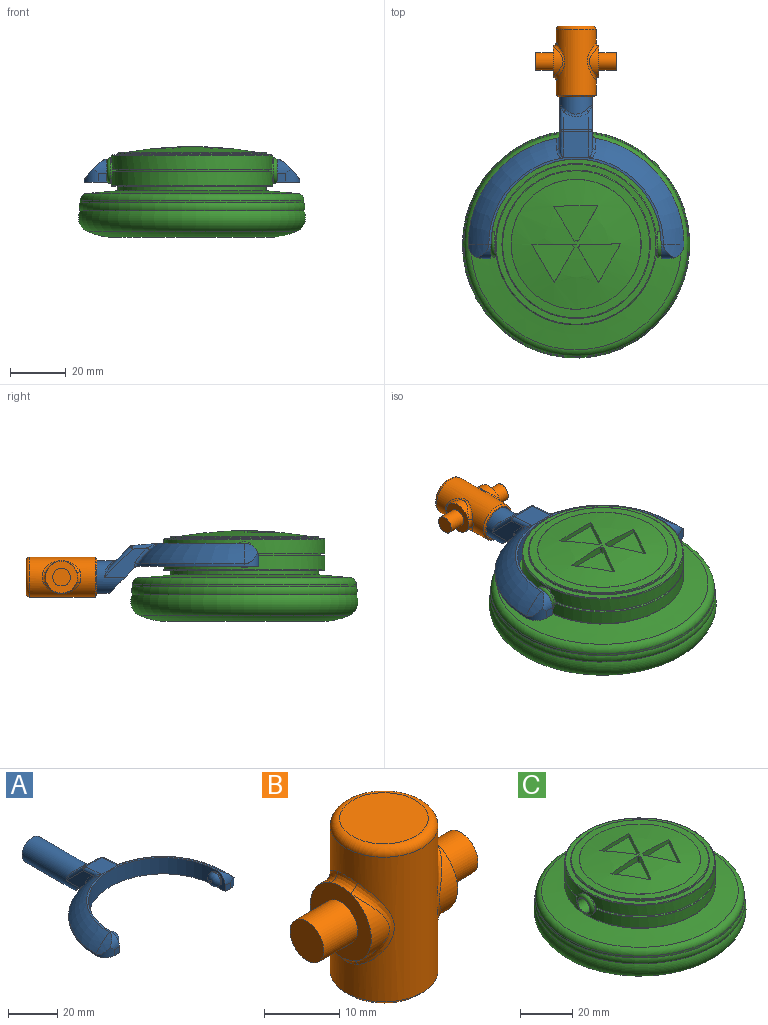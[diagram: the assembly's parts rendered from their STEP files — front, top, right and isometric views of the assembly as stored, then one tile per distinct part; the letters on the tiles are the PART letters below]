
ASSEMBLY  parts=3 mates=2
PART A: 48 faces, bbox 77.3x80.8x18.2 mm
  f0: plane 11.99x9.83mm, normal (0,-0.71,-0.71), area 141.5mm2, adj f1,f2,f9,f30,f43,f46
  f1: plane 15.39x10.49mm, normal (-1,0,0), area 63.5mm2, adj f0,f30,f32,f36,f46,f47
  f2: plane 15.39x10.49mm, normal (1,0,0), area 63.5mm2, adj f0,f30,f34,f39,f43,f44
  f3: plane 9.14x6.37mm, normal (0,0.71,0.71), area 67.6mm2, adj f35,f36,f39,f40
  f4: cylinder r=38.61mm len=37.99mm, axis (0,0,-1), area 42.6mm2, adj f6,f9,f17,f46,f47
  f5: torus R=19.3mm, axis (0,0,-1), area 507.8mm2, adj f10,f11,f12,f29,f42,f44
  f6: torus R=19.3mm, axis (0,0,-1), area 507.8mm2, adj f4,f11,f15,f28,f45,f47
  f7: cylinder r=30.48mm len=60.96mm, axis (0,0,-1), area 746.6mm2, adj f8,f9,f11,f14,f21,f24
  f8: plane 8.13x5.08mm, normal (-1,0,0), area 19.9mm2, adj f7,f9,f13,f19,f24
  f9: plane 77.22x43.73mm, normal (0,0,-1), area 956.2mm2, adj f0,f4,f7,f8,f10,f13,f14,f16
  f10: cylinder r=38.61mm len=37.99mm, axis (0,0,-1), area 42.6mm2, adj f5,f9,f20,f43,f44
  f11: plane 62.55x30.95mm, normal (0,0,1), area 75mm2, adj f5,f6,f7,f18,f19,f27
  f12: cylinder r=22.71mm len=7.33mm, axis (0,1,0), area 24.8mm2, adj f5,f19,f20
  f13: plane 3.05x3.05mm, normal (0,-1,0), area 9.3mm2, adj f8,f9,f19,f20
  f14: plane 8.13x5.08mm, normal (1,0,0), area 19.9mm2, adj f7,f9,f16,f18,f21
  f15: cylinder r=22.71mm len=7.33mm, axis (0,1,0), area 24.8mm2, adj f6,f17,f18
  f16: plane 3.05x3.05mm, normal (0,-1,0), area 9.3mm2, adj f9,f14,f17,f18
  f17: cylinder r=5.08mm len=5.08mm, axis (0,0,-1), area 21.9mm2, adj f4,f9,f15,f16,f18
  f18: cylinder r=5.08mm len=5.08mm, axis (-1,0,0), area 21.9mm2, adj f11,f14,f15,f16,f17
  f19: cylinder r=5.08mm len=5.08mm, axis (-1,0,0), area 21.9mm2, adj f8,f11,f12,f13,f20
  f20: cylinder r=5.08mm len=5.08mm, axis (0,0,-1), area 21.9mm2, adj f9,f10,f12,f13,f19
  f21: cylinder r=3.17mm len=6.35mm, axis (-1,0,0), area 12.7mm2, adj f7,f14,f23
  f22: plane 1.27x1.27mm, normal (1,0,0), area 1.3mm2, adj f23
  f23: torus R=0.64mm, axis (1,0,0), area 56.5mm2, adj f21,f22
  f24: cylinder r=3.17mm len=6.35mm, axis (1,0,0), area 12.7mm2, adj f7,f8,f26
  f25: plane 1.27x1.27mm, normal (-1,0,0), area 1.3mm2, adj f26
  f26: torus R=0.64mm, axis (-1,0,0), area 56.5mm2, adj f24,f25
  f27: plane 9.86x9.36mm, normal (0,0.09,1), area 85.6mm2, adj f11,f28,f29,f32,f34,f35,f42,f45
  f28: plane 1.04x0.17mm, normal (0,-1,0), area 0mm2, adj f6,f27,f45
  f29: plane 1.04x0.17mm, normal (0,-1,0), area 0mm2, adj f5,f27,f42
  f30: cylinder r=5.84mm len=33.01mm, axis (0,-1,0), area 1029.7mm2, adj f0,f1,f2,f31,f38,f40,f41
  f31: plane 11.68x11.68mm, normal (0,1,0), area 107.2mm2, adj f30
  f32: cylinder r=1.27mm len=9.13mm, axis (0,-1,0.09), area 14.4mm2, adj f1,f27,f33,f45
  f33: sphere r=1.27mm, area 1.5mm2, adj f32,f35,f36
  f34: cylinder r=1.27mm len=9.13mm, axis (0,1,-0.09), area 14.4mm2, adj f2,f27,f37,f42
  f35: cylinder r=1.27mm len=9.14mm, axis (-1,0,0), area 8.1mm2, adj f3,f27,f33,f37
  f36: cylinder r=1.27mm len=10.91mm, axis (0,-0.71,0.71), area 23.1mm2, adj f1,f3,f33,f38
  f37: sphere r=1.27mm, area 1.5mm2, adj f34,f35,f39
  f38: bspline ~4.55x2.75mm, area 2.3mm2, adj f30,f36,f40
  f39: cylinder r=1.27mm len=10.91mm, axis (0,0.71,-0.71), area 23.1mm2, adj f2,f3,f37,f41
  f40: bspline ~9.14x2.56mm, area 10.7mm2, adj f3,f30,f38,f41
  f41: bspline ~5.23x3.53mm, area 2.3mm2, adj f30,f39,f40
  f42: bspline ~4.62x3.14mm, area 5.2mm2, adj f5,f27,f29,f34,f44
  f43: cylinder r=1.27mm len=1.74mm, axis (0,0,-1), area 1.9mm2, adj f0,f2,f9,f10,f44
  f44: bspline ~8.6x7.86mm, area 11.9mm2, adj f2,f5,f10,f42,f43
  f45: bspline ~4.62x3.14mm, area 5.2mm2, adj f6,f27,f28,f32,f47
  f46: cylinder r=1.27mm len=1.74mm, axis (0,0,-1), area 1.9mm2, adj f0,f1,f4,f9,f47
  f47: bspline ~8.6x7.86mm, area 11.9mm2, adj f1,f4,f6,f45,f46
PART B: 25 faces, bbox 28.9x15.5x25.4 mm
  f0: cylinder r=5.71mm len=10.81mm, axis (-1,0,0), area 26.2mm2, adj f5,f15
  f1: cylinder r=5.71mm len=10.81mm, axis (-1,0,0), area 26.2mm2, adj f8,f11
  f2: cylinder r=7.14mm len=23.5mm, axis (0,0,-1), area 763.2mm2, adj f9,f10,f11,f12,f13,f14,f15,f16
  f3: plane 11.75x11.75mm, normal (0,0,1), area 108.4mm2, adj f17
  f4: plane 13.02x13.02mm, normal (0,0,-1), area 16.3mm2, adj f22,f24
  f5: plane 11.46x11.46mm, normal (1,0,0), area 70.9mm2, adj f0,f6,f13,f16,f18
  f6: cylinder r=5.71mm len=10.81mm, axis (-1,0,0), area 26.2mm2, adj f5,f14
  f7: cylinder r=5.71mm len=10.81mm, axis (-1,0,0), area 26.2mm2, adj f8,f10
  f8: plane 11.46x11.46mm, normal (-1,0,0), area 70.9mm2, adj f1,f7,f9,f12,f20
  f9: bspline ~4.64x1.73mm, area 6.5mm2, adj f2,f8,f10,f11
  f10: bspline ~13.62x4.91mm, area 20.7mm2, adj f2,f7,f9,f12
  f11: bspline ~13.6x4.87mm, area 20.7mm2, adj f1,f2,f9,f12
  f12: bspline ~4.64x1.73mm, area 6.5mm2, adj f2,f8,f10,f11
  f13: bspline ~4.64x1.73mm, area 6.5mm2, adj f2,f5,f14,f15
  f14: bspline ~13.62x4.91mm, area 20.7mm2, adj f2,f6,f13,f16
  f15: bspline ~13.6x4.87mm, area 20.7mm2, adj f0,f2,f13,f16
  f16: bspline ~4.64x1.73mm, area 6.5mm2, adj f2,f5,f14,f15
  f17: torus R=5.87mm, axis (0,0,1), area 83.8mm2, adj f2,f3
  f18: cylinder r=3.17mm len=6.35mm, axis (-1,0,0), area 126.7mm2, adj f5,f19
  f19: plane 6.35x6.35mm, normal (1,0,0), area 31.7mm2, adj f18
  f20: cylinder r=3.17mm len=6.35mm, axis (1,0,0), area 126.7mm2, adj f8,f21
  f21: plane 6.35x6.35mm, normal (-1,0,0), area 31.7mm2, adj f20
  f22: cylinder r=6.1mm len=22.86mm, axis (0,0,-1), area 875.6mm2, adj f4,f23
  f23: plane 12.19x12.19mm, normal (0,0,-1), area 116.7mm2, adj f22
  f24: cone r=7.14mm half-angle=45deg, axis (0,0,1), area 38.5mm2, adj f2,f4
PART C: 48 faces, bbox 96.2x96.2x32.5 mm
  f0: cylinder r=28.88mm len=57.76mm, axis (0,0,-1), area 856mm2, adj f1,f2,f38,f39,f44
  f1: plane 57.03x24.32mm, normal (0,0,1), area 101.1mm2, adj f0,f3,f38,f39
  f2: plane 57.03x24.32mm, normal (0,0,1), area 101.1mm2, adj f0,f4,f38,f39
  f3: cylinder r=27.61mm len=54.46mm, axis (0,0,-1), area 49.3mm2, adj f1,f6,f38,f39
  f4: cylinder r=27.61mm len=54.46mm, axis (0,0,-1), area 49.3mm2, adj f2,f5,f38,f39
  f5: plane 57.03x24.32mm, normal (0,0,-1), area 101.1mm2, adj f4,f7,f38,f39
  f6: plane 57.03x24.32mm, normal (0,0,-1), area 101.1mm2, adj f3,f7,f38,f39
  f7: cylinder r=28.88mm len=57.76mm, axis (0,0,-1), area 856mm2, adj f5,f6,f38,f39,f45
  f8: sphere r=135.39mm, area 1385.3mm2, adj f22,f23,f24,f25,f27,f28,f29,f30
  f9: plane 39.33x39.33mm, normal (0,0,-1), area 1214.6mm2, adj f10
  f10: torus R=20.12mm, axis (0,0,-1), area 1429.3mm2, adj f9,f11
  f11: torus R=27.74mm, axis (0,0,-1), area 3542.1mm2, adj f10,f12
  f12: torus R=35.36mm, axis (0,0,-1), area 2180.1mm2, adj f11,f13
  f13: torus R=37.35mm, axis (0,0,-1), area 734.6mm2, adj f12,f14
  f14: cylinder r=40.06mm len=80.11mm, axis (0,0,-1), area 213.3mm2, adj f13,f18
  f15: cone r=26.57mm half-angle=85deg, axis (0,0,-1), area 2265mm2, adj f16,f18
  f16: cylinder r=26.57mm len=53.14mm, axis (0,0,-1), area 265mm2, adj f15,f17
  f17: plane 57.25x57.25mm, normal (0,0,-1), area 356.7mm2, adj f16,f44
  f18: torus R=37.52mm, axis (0,0,1), area 928.6mm2, adj f14,f15
  f19: cone r=26.57mm half-angle=87deg, axis (0,0,-1), area 475.4mm2, adj f46,f47
  f20: cylinder r=26.57mm len=53.14mm, axis (0,0,-1), area 92.3mm2, adj f21,f46
  f21: plane 57.25x57.25mm, normal (0,0,1), area 356.7mm2, adj f20,f45
  f22: cylinder r=1.27mm len=2.53mm, axis (0,0,1), area 3.4mm2, adj f8,f23,f25,f26
  f23: plane 14.6x2.53mm, normal (0.01,-1,0), area 32.2mm2, adj f8,f22,f24,f26
  f24: plane 13.68x8.05mm, normal (0.86,0.51,0), area 28mm2, adj f8,f23,f25,f26
  f25: plane 12.71x7.2mm, normal (-0.87,0.49,0), area 32.2mm2, adj f8,f22,f24,f26
  f26: plane 15.25x13.8mm, normal (0,0,1), area 108.3mm2, adj f22,f23,f24,f25
  f27: cylinder r=1.27mm len=2.53mm, axis (0,0,1), area 3.4mm2, adj f8,f28,f30,f31
  f28: plane 12.59x7.41mm, normal (0.86,0.51,0), area 32.2mm2, adj f8,f27,f29,f31
  f29: plane 13.81x7.82mm, normal (-0.87,0.49,0), area 28mm2, adj f8,f28,f30,f31
  f30: plane 14.6x2.53mm, normal (0.01,-1,0), area 32.2mm2, adj f8,f27,f29,f31
  f31: plane 15.23x13.81mm, normal (0,0,1), area 108.3mm2, adj f27,f28,f29,f30
  f32: plane 12.71x7.2mm, normal (-0.87,0.49,0), area 32.2mm2, adj f8,f33,f35,f36
  f33: plane 15.87x1.84mm, normal (0.01,-1,0), area 28mm2, adj f8,f32,f34,f36
  f34: plane 12.59x7.41mm, normal (0.86,0.51,0), area 32.2mm2, adj f8,f33,f35,f36
  f35: cylinder r=1.27mm len=2.53mm, axis (0,0,1), area 3.4mm2, adj f8,f32,f34,f36
  f36: plane 15.87x12.72mm, normal (0,0,1), area 108.3mm2, adj f32,f33,f34,f35
  f37: plane 6.6x6.6mm, normal (1,0,0), area 2.6mm2, adj f42,f43
  f38: cylinder r=4.57mm len=9.14mm, axis (-1,0,0), area 16.3mm2, adj f0,f1,f2,f3,f4,f5,f6,f7
  f39: cylinder r=4.57mm len=9.14mm, axis (-1,0,0), area 16.3mm2, adj f0,f1,f2,f3,f4,f5,f6,f7
  f40: plane 6.6x6.6mm, normal (-1,0,0), area 2.6mm2, adj f41,f43
  f41: torus R=3.3mm, axis (1,0,0), area 51.5mm2, adj f39,f40
  f42: torus R=3.3mm, axis (1,0,0), area 51.5mm2, adj f37,f38
  f43: cylinder r=3.17mm len=60.96mm, axis (1,0,0), area 1216.1mm2, adj f37,f40
  f44: torus R=28.63mm, axis (0,0,1), area 72.2mm2, adj f0,f17
  f45: torus R=28.63mm, axis (0,0,-1), area 72.2mm2, adj f7,f21
  f46: torus R=26.31mm, axis (0,0,1), area 64.2mm2, adj f19,f20
  f47: torus R=23.29mm, axis (0,0,1), area 4.5mm2, adj f8,f19
PLACE A t=(32.34,27.52,20.85)mm
PLACE B rot(axis=(-1,0,0),90deg) t=(32.34,80.3,16.88)mm
PLACE C t=(32.34,27.52,33.52)mm
MATE revolute A.f24 <-> C.f38  axis (-1,0,0) through (62.82,27.52,24.92)mm
MATE revolute B.f2 <-> A.f30  axis (0,-1,0) through (32.34,103.16,16.88)mm
